# Revit family: Air_Conditioner-Packaged-Friedrich-Vert_I_Pak-Heat_Pump_VHA18
name_source: partatom
category: Mechanical Equipment
revit_build: Autodesk Revit 2018 (Build: 20190510_1515(x64)
units: mm (PartAtom-declared; Revit-internal decimal feet)

## family parameters
Always vertical = Yes
Cut with Voids When Loaded = No
OmniClass Number = 23.75.10.24.21.27.21
OmniClass Title = Packaged Terminal Air Conditioning Units
Part Type = Normal
Room Calculation Point = No
Round Connector Dimension = Use Radius
Shared = No
Work Plane-Based = No

## types (9) — shared parameters
04 CSI = 23 81 00
95 CSI = 15730
Air Flow = 950 CFM
Air Supply Radius = 5.00"
Assembly Code = D3050
COP = 3.3
Condensate Drain Flow = 0 GPM
Connector Description = Supply Air Outlet Connection
Cooling Nominal Input Power = 1670 W
Depth = 23.00"
Description = Single Package Vertical Air Conditioner
Drain Radius = 0.38"
EER Rating = 11
Frame Material = Metal - Friedrich - Stainless Steel
Frequency = 60 Hz
Heating Nominal Input Power = 1480 W
Height = 47.93"
Indoor Motor Amperage = 0 A
Indoor Motor HP = 1/4
Installation and Maintenance URL = http://friedrich.com
Load Classification = HVAC
Locked Rotor Current = 37 A
Manufacturer = Friedrich
Max ESP = 0.40"
Model = VEH Heat Pump Models
Number of Poles = 1
Outdoor Motor Amperage = 2 A
Outdoor Motor HP = 1/4
Phase = 1
Power Factor = 1
Product Line = Vert-I-Pak
Product Page URL = http://friedrich.com
Product data url = https://bimobject.com
R 410A Charge Capacity = 57
Refrigerant Charge = 3.56 lb
Sensible Heat Ratio = 0.7
Subcategory = Commercial Air Conditioning
Submittal URL = http://friedrich.com
Total Cooling Capacity = 18400.0 Btu/h
Total Heating Capacity = 16700.0 Btu/h
URL = http://friedrich.com
Vent Airflow = 60 CFM
Warranty URL = http://friedrich.com
Width = 23.00"
ecoScorecard Product Page = http://ecoscorecard.com

## per-type parameters (varying)
| type | Amperage | Electric Heat Wattage | Full Load Current | Heat Pump Current | Heater Size | Voltage | Voltage Range | Weight |
| VHA18K25RTL  -  230 V  -  18400 BTUh Cooling - 16700 BTUh Heating | 8 A | 2050 W | 8 A | 7 A | 2.5 KW | 230 V | 197-253 V | 190.00 lb |
| VHA18K34RTL  -  230 V  -  18400 BTUh Cooling - 16700 BTUh Heating | 8 A | 2780 W | 8 A | 7 A | 3.4 KW | 230 V | 197-253 V | 190.00 lb |
| VHA18K50RTL  -  230 V  -  18400 BTUh Cooling - 16700 BTUh Heating | 8 A | 4090 W | 8 A | 7 A | 5.0 KW | 230 V | 197-253 V | 190.00 lb |
| VHA18K25RTL  -  208 V  -  18400 BTUh Cooling - 16700 BTUh Heating | 8 A | 2050 W | 8 A | 7 A | 2.5 KW | 208 V | 197-253 V | 190.00 lb |
| VHA18K34RTL  -  208 V  -  18400 BTUh Cooling - 16700 BTUh Heating | 8 A | 2780 W | 8 A | 7 A | 3.4 KW | 208 V | 197-253 V | 190.00 lb |
| VHA18K50RTL  -  208 V  -  18400 BTUh Cooling - 16700 BTUh Heating | 8 A | 4090 W | 8 A | 7 A | 5.0 KW | 208 V | 197-253 V | 190.00 lb |
| VHA18R25RTM  -  265 V  -  18400 BTUh Cooling - 16700 BTUh Heating | 7 A | 2500 W | 7 A | 6 A | 2.5 KW | 265 V | 239-292 V | 192.00 lb |
| VHA18R34RTM  -  265 V  -  18400 BTUh Cooling - 16700 BTUh Heating | 7 A | 3400 W | 7 A | 6 A | 3.4 KW | 265 V | 239-292 V | 192.00 lb |
| VHA18R50RTM  -  265 V  -  18400 BTUh Cooling - 16700 BTUh Heating | 7 A | 5000 W | 7 A | 6 A | 5.0 KW | 265 V | 239-292 V | 192.00 lb |

## geometry (parser evidence)
native form markers: Blend x6, Sweep x4
no freeform markers — native parametric forms only
